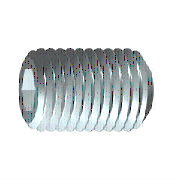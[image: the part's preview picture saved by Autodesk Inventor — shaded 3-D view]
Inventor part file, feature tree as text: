
AUTODESK INVENTOR PART (.ipt)
format: ipt  version: 2013 (Build 170138000, 138)  size: 173,568 bytes
history: native  units: mm (DEFAULTED — no unit token found)
features: sketch x2, extrude x1, other x1, plane x1
ambient origin geometry x8: Origin, YZ Plane, XZ Plane, XY Plane, X Axis, Y Axis, Z Axis, Center Point
bodies: Solid1 (feature_tree), Body (feature_tree)
feature tree (5):
  extrude  "Slot"  TaperAngle=60.0deg  [1 undecoded]
  other  "Work Axis1"
  plane  "Work Plane1"
  sketch  "Sketch1"  dims[d0=2.032mm d1=60.0deg]
  sketch  "Sketch2"  dims[d2=4.1656mm d3=2.287693mm d6=90.0deg d4=4.7625mm d5=10.297443mm d7=2.0828mm d8=2.032mm d9=0.0mm d10=1.0414mm d11=45.0deg d12=0.42926mm d13=45.0deg d14=4.7625mm d15=0.0mm d16=0.0mm d33=1.0414mm d34=0.42926mm d35=0.0mm d37=0.0mm]
note: 1 required parameter value undecoded (feature->parameter linkage not recoverable at this tier; creation-order binding heuristic only, values carry confidence <= 0.55)
